# Revit family: Banco Volga
name_source: partatom
category: Furniture
units: mm (PartAtom-declared; Revit-internal decimal feet)

## family parameters
Always vertical = Yes
Cut with Voids When Loaded = No
OmniClass Number = 23.40.20.00
OmniClass Title = General Furniture and Specialties
Room Calculation Point = No
Shared = No
Work Plane-Based = No

## types (4) — shared parameters
A = 2 m
B = 0.6 m
Material listones = <By Category>
zero-valued in all types: Default Elevation

## per-type parameters (varying)
| type | H | Material banco | UM369-2000mm | UM369G-2000mm | UM369GLM-2000 | UM369LM-2000 |
| Banco Volga-UM369G-2000mm | 0.45 m | <By Category> | No | Yes | No | No |
| Banco Volga-UM369GLM-2000mm | 0.48 m | <By Category> | No | No | Yes | No |
| Banco Volga-UM369-2000mm | 0.45 m | <By Category> | Yes | No | No | No |
| Banco Volga-UM369LM-2000mm | 0.48 m | Air Openings | No | No | No | Yes |

## geometry (parser evidence)
native form markers: Blend x4, Sweep x9
no freeform markers — native parametric forms only
